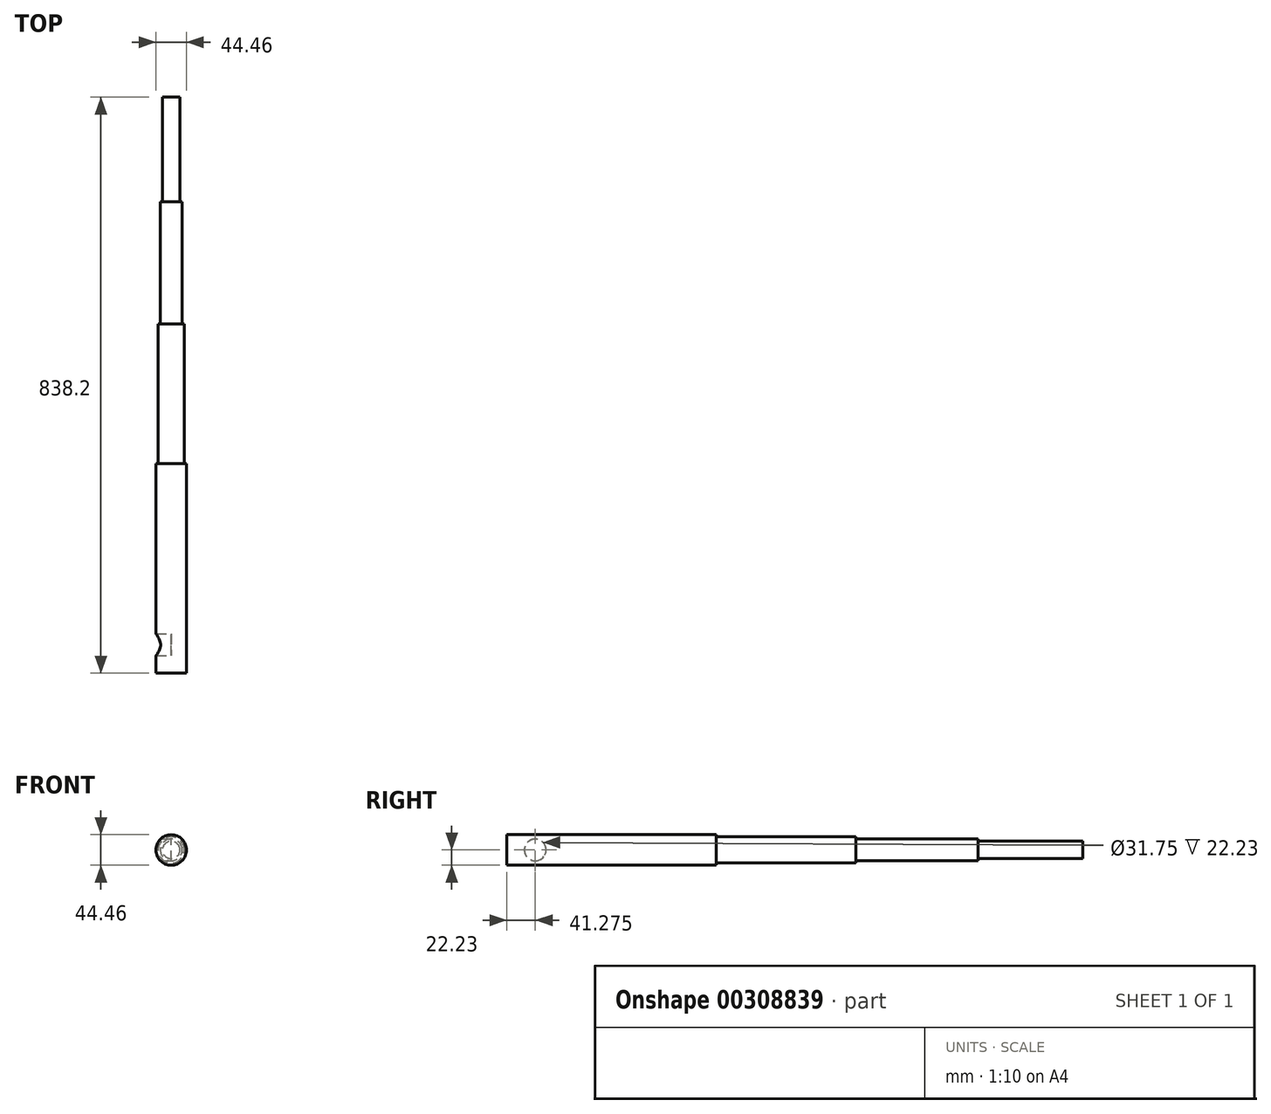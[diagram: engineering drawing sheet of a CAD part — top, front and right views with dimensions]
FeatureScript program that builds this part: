
annotation { "Feature Type Name" : "Feature", "Feature Type Description" : "" }
export const myFeature = defineFeature(function(context is Context, id is Id, definition is map)
    precondition{}
    {
        {
            var Q0;
            Q0=qCreatedBy(makeId("Front.planeOp"),FACE);
            var sketch = newSketch(context, id + "F0", { "sketchPlane" : qUnion([Q0])});
            skCircle(sketch, "E0", {"center": v(0, 0) * mm, "radius": 12.7 * mm});
            skSolve(sketch);
        }
        {
            var Q0;
            Q0=makeQuery(id+"F0.imprint","IMPRINT",FACE,{"disambiguationData":[TD([[makeQuery(id+"F0.imprint","IMPRINT",EDGE,{"derivedFrom":sQuery(id+"F0.wireOp",EDGE,"E0")}),1.0]])]});
            extrude(context, id + "F1", {"entities" : qUnion([Q0]), "depth" : 152.4 * mm});
        }
        {
            var Q0;
            Q0=makeQuery(id+"F1.opExtrude","CAP_FACE",FACE,{"disambiguationData":[OSD([sQuery(id+"F0.wireOp",EDGE,"E0")])],"isStart":false});
            var sketch = newSketch(context, id + "F2", { "sketchPlane" : qUnion([Q0])});
            skCircle(sketch, "E1", {"center": v(0, 0) * mm, "radius": 15.88 * mm});
            skSolve(sketch);
        }
        {
            var Q0;
            Q0=makeQuery(id+"F2.imprint","IMPRINT",FACE,{"disambiguationData":[TD([[makeQuery(id+"F2.imprint","IMPRINT",EDGE,{"derivedFrom":makeQuery(id+"F1.opExtrude","CAP_EDGE",EDGE,{"disambiguationData":[OSD([sQuery(id+"F0.wireOp",EDGE,"E0")])],"isStart":false})}),1.0]])]});
            var Q1;
            Q1=makeQuery(id+"F2.imprint","IMPRINT",FACE,{"disambiguationData":[TD([[makeQuery(id+"F2.imprint","IMPRINT",EDGE,{"derivedFrom":sQuery(id+"F2.wireOp",EDGE,"E1")}),1.0]])]});
            extrude(context, id + "F3", {"entities" : qUnion([Q0, Q1]), "operationType" : NewBodyOperationType.ADD, "depth" : 177.8 * mm});
        }
        {
            var Q0;
            Q0=makeQuery(id+"F3.opExtrude","CAP_FACE",FACE,{"disambiguationData":[OSD([sQuery(id+"F2.wireOp",EDGE,"E1")])],"isStart":false});
            var sketch = newSketch(context, id + "F4", { "sketchPlane" : qUnion([Q0])});
            skCircle(sketch, "E2", {"center": v(0, 0) * mm, "radius": 19.05 * mm});
            skSolve(sketch);
        }
        {
            var Q0;
            Q0=makeQuery(id+"F4.imprint","IMPRINT",FACE,{"disambiguationData":[TD([[makeQuery(id+"F4.imprint","IMPRINT",EDGE,{"derivedFrom":makeQuery(id+"F3.opExtrude","CAP_EDGE",EDGE,{"disambiguationData":[OSD([sQuery(id+"F2.wireOp",EDGE,"E1")])],"isStart":false})}),1.0]])]});
            var Q1;
            Q1=makeQuery(id+"F4.imprint","IMPRINT",FACE,{"disambiguationData":[TD([[makeQuery(id+"F4.imprint","IMPRINT",EDGE,{"derivedFrom":sQuery(id+"F4.wireOp",EDGE,"E2")}),1.0]])]});
            extrude(context, id + "F5", {"entities" : qUnion([Q0, Q1]), "operationType" : NewBodyOperationType.ADD, "depth" : 203.2 * mm});
        }
        {
            var Q0;
            Q0=makeQuery(id+"F5.opExtrude","CAP_FACE",FACE,{"disambiguationData":[OSD([sQuery(id+"F4.wireOp",EDGE,"E2")])],"isStart":false});
            var sketch = newSketch(context, id + "F6", { "sketchPlane" : qUnion([Q0])});
            skCircle(sketch, "E3", {"center": v(0, 0) * mm, "radius": 22.23 * mm});
            skSolve(sketch);
        }
        {
            var Q0;
            Q0=makeQuery(id+"F6.imprint","IMPRINT",FACE,{"disambiguationData":[TD([[makeQuery(id+"F6.imprint","IMPRINT",EDGE,{"derivedFrom":makeQuery(id+"F5.opExtrude","CAP_EDGE",EDGE,{"disambiguationData":[OSD([sQuery(id+"F4.wireOp",EDGE,"E2")])],"isStart":false})}),1.0]])]});
            var Q1;
            Q1=makeQuery(id+"F6.imprint","IMPRINT",FACE,{"disambiguationData":[TD([[makeQuery(id+"F6.imprint","IMPRINT",EDGE,{"derivedFrom":sQuery(id+"F6.wireOp",EDGE,"E3")}),1.0]])]});
            extrude(context, id + "F7", {"entities" : qUnion([Q0, Q1]), "operationType" : NewBodyOperationType.ADD, "depth" : 304.8 * mm});
        }
        {
            var Q0;
            Q0=qCreatedBy(makeId("Right.planeOp"),FACE);
            var sketch = newSketch(context, id + "F8", { "sketchPlane" : qUnion([Q0])});
            skCircle(sketch, "E4", {"center": v(-796.93, 0) * mm, "radius": 15.88 * mm});
            skSolve(sketch);
        }
        {
            var Q0;
            Q0 = qSketchRegion(id + "F8", true);
            extrude(context, id + "F9", {"entities" : qUnion([Q0]), "operationType" : NewBodyOperationType.REMOVE, "oppositeDirection" : true, "depth" : 25.4 * mm});
        }
    });
